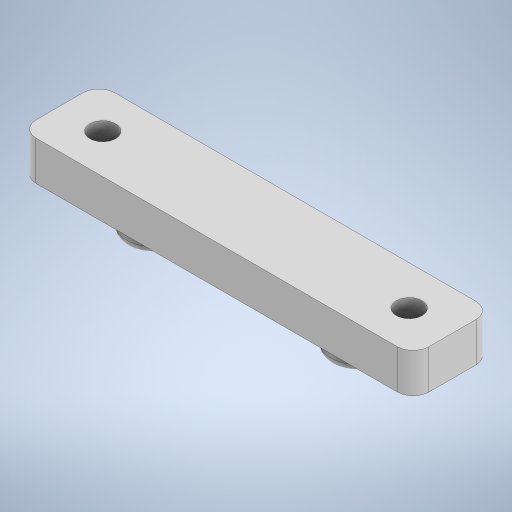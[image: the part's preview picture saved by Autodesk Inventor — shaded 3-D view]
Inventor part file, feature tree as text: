
AUTODESK INVENTOR PART (.ipt)
format: ipt  version: 2024 (Build 280153000, 153)  size: 257,024 bytes
history: native  units: mm
features: extrude x2, other x1, sketch x1, fillet x1
ambient origin geometry x8: Origin, YZ Plane, XZ Plane, XY Plane, X Axis, Y Axis, Z Axis, Center Point
bodies: Body1 (feature_tree)
feature tree (5):
  other  "Твердое тело1"
  sketch  "Эскиз1"
  extrude  "Выдавливание1"  Depth=7.0mm
  extrude  "Выдавливание2"  Depth=7.0mm
  fillet  "Сопряжение1"  Radius=19.0mm
